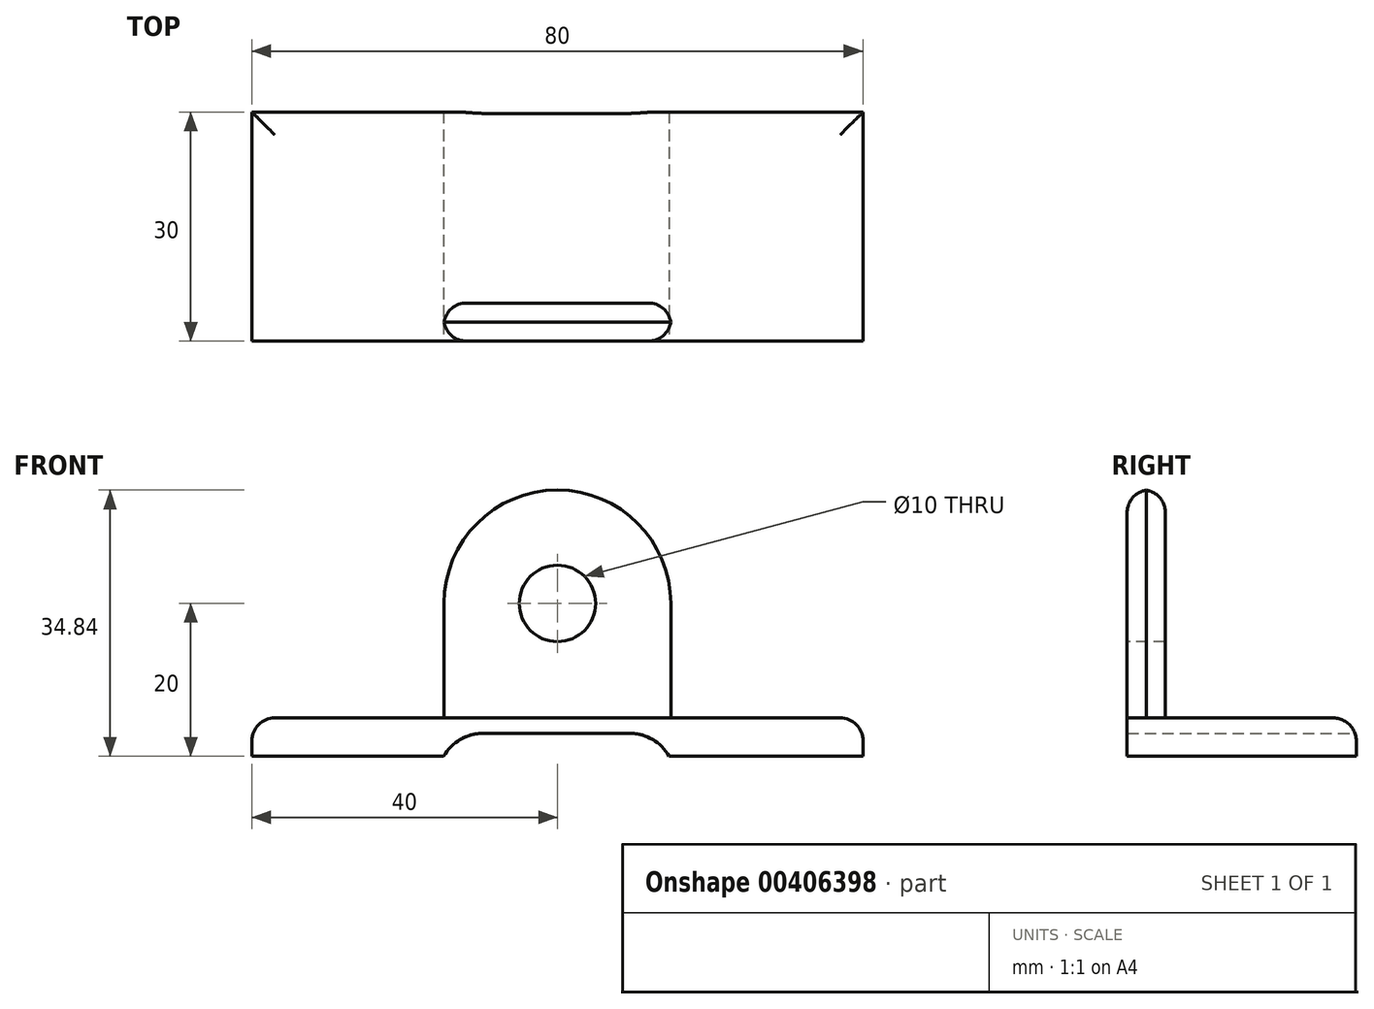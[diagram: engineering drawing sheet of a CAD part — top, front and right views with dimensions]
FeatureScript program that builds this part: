
annotation { "Feature Type Name" : "Feature", "Feature Type Description" : "" }
export const myFeature = defineFeature(function(context is Context, id is Id, definition is map)
    precondition{}
    {
        {
            var Q0;
            Q0=qCreatedBy(makeId("Top.planeOp"),FACE);
            var sketch = newSketch(context, id + "F0", { "sketchPlane" : qUnion([Q0])});
            skLineSegment(sketch, "E0.bottom", {"start": v(40, -15) * mm, "end": v(-40, -15) * mm});
            skLineSegment(sketch, "E0.top", {"start": v(40, 15) * mm, "end": v(-40, 15) * mm});
            skLineSegment(sketch, "E0.left", {"start": v(40, -15) * mm, "end": v(40, 15) * mm});
            skLineSegment(sketch, "E0.right", {"start": v(-40, -15) * mm, "end": v(-40, 15) * mm});
            skPoint(sketch, "E0.middle", {"position": v(0, 0) * mm});
            skSolve(sketch);
        }
        {
            var Q0;
            Q0=makeQuery(id+"F0.imprint","IMPRINT",FACE,{"disambiguationData":[TD([[makeQuery(id+"F0.imprint","IMPRINT",EDGE,{"derivedFrom":sQuery(id+"F0.wireOp",EDGE,"E0.bottom")}),-1.0]])]});
            extrude(context, id + "F1", {"entities" : qUnion([Q0]), "depth" : 5 * mm});
        }
        {
            var Q0;
            Q0=makeQuery(id+"F1.opExtrude","SWEPT_FACE",FACE,{"disambiguationData":[OSD([sQuery(id+"F0.wireOp",EDGE,"E0.bottom")])]});
            var sketch = newSketch(context, id + "F2", { "sketchPlane" : qUnion([Q0])});
            skLineSegment(sketch, "E1", {"start": v(-14.89, 0) * mm, "end": v(-14.89, 20) * mm});
            skArc(sketch, "E2", {"start": v(14.89, 20) * mm, "mid": v(0, 34.89) * mm, "end": v(-14.89, 20) * mm});
            skLineSegment(sketch, "E3", {"start": v(14.89, 20) * mm, "end": v(14.89, 0) * mm});
            skLineSegment(sketch, "E4", {"start": v(14.89, 0) * mm, "end": v(-14.89, 0) * mm});
            skCircle(sketch, "E5", {"center": v(0, 20) * mm, "radius": 5 * mm});
            skSolve(sketch);
        }
        {
            var Q0;
            {var subQ1=sQuery(id+"F2.wireOp",EDGE,"E2");Q0=makeQuery(id+"F2.imprint","IMPRINT",FACE,{"disambiguationData":[TD([[makeQuery(id+"F2.imprint","IMPRINT",EDGE,{"derivedFrom":subQ1}),1.0]])]});}
            extrude(context, id + "F3", {"entities" : qUnion([Q0]), "oppositeDirection" : true, "depth" : 5 * mm});
        }
        {
            var Q0;
            Q0=makeQuery(id+"F1.opExtrude","SWEPT_FACE",FACE,{"disambiguationData":[OSD([sQuery(id+"F0.wireOp",EDGE,"E0.bottom")])]});
            var sketch = newSketch(context, id + "F4", { "sketchPlane" : qUnion([Q0])});
            skLineSegment(sketch, "E6.bottom", {"start": v(-14.89, 0) * mm, "end": v(14.63, 0) * mm});
            skLineSegment(sketch, "E6.top", {"start": v(-14.89, 3) * mm, "end": v(14.63, 3) * mm});
            skLineSegment(sketch, "E6.left", {"start": v(-14.89, 0) * mm, "end": v(-14.89, 3) * mm});
            skLineSegment(sketch, "E6.right", {"start": v(14.63, 0) * mm, "end": v(14.63, 3) * mm});
            skSolve(sketch);
        }
        {
            var Q0;
            Q0=makeQuery(id+"F4.imprint","IMPRINT",FACE,{"disambiguationData":[TD([[makeQuery(id+"F4.imprint","IMPRINT",EDGE,{"derivedFrom":sQuery(id+"F4.wireOp",EDGE,"E6.bottom")}),-1.0]])]});
            extrude(context, id + "F5", {"entities" : qUnion([Q0]), "operationType" : NewBodyOperationType.REMOVE, "endBound" : BoundingType.THROUGH_ALL, "oppositeDirection" : true, "depth" : 25 * mm});
        }
        {
            var Q0;
            Q0=makeQuery(id+"F5.boolean.opBoolean","COPY",EDGE,{"derivedFrom":makeQuery(id+"F5.opExtrude","SWEPT_EDGE",EDGE,{"disambiguationData":[OSD([sQuery(id+"F4.wireOp",EDGE,"E6.top"),sQuery(id+"F4.wireOp",EDGE,"E6.left")])]})});
            var Q1;
            Q1=makeQuery(id+"F5.boolean.opBoolean","COPY",EDGE,{"derivedFrom":makeQuery(id+"F5.opExtrude","SWEPT_EDGE",EDGE,{"disambiguationData":[OSD([sQuery(id+"F4.wireOp",EDGE,"E6.top"),sQuery(id+"F4.wireOp",EDGE,"E6.right")])]})});
            fillet(context, id + "F6", {"entities" : qUnion([Q0, Q1]), "radius" : 6 * mm, "tangentPropagation" : true, "allowEdgeOverflow" : false});
        }
        {
            var Q0;
            Q0=makeQuery(id+"F3.opExtrude","CAP_EDGE",EDGE,{"disambiguationData":[OSD([sQuery(id+"F2.wireOp",EDGE,"E3")])],"isStart":true});
            var Q1;
            Q1=makeQuery(id+"F3.opExtrude","CAP_EDGE",EDGE,{"disambiguationData":[OSD([sQuery(id+"F2.wireOp",EDGE,"E3")])],"isStart":false});
            var Q2;
            Q2=makeQuery(id+"F1.opExtrude","CAP_EDGE",EDGE,{"disambiguationData":[OSD([sQuery(id+"F0.wireOp",EDGE,"E0.left")])],"isStart":false});
            var Q3;
            Q3=makeQuery(id+"F1.opExtrude","CAP_EDGE",EDGE,{"disambiguationData":[OSD([sQuery(id+"F0.wireOp",EDGE,"E0.top")])],"isStart":false});
            var Q4;
            Q4=makeQuery(id+"F1.opExtrude","CAP_EDGE",EDGE,{"disambiguationData":[OSD([sQuery(id+"F0.wireOp",EDGE,"E0.right")])],"isStart":false});
            fillet(context, id + "F7", {"entities" : qUnion([Q0, Q1, Q2, Q3, Q4]), "radius" : 3 * mm, "tangentPropagation" : true, "allowEdgeOverflow" : false});
        }
    });
